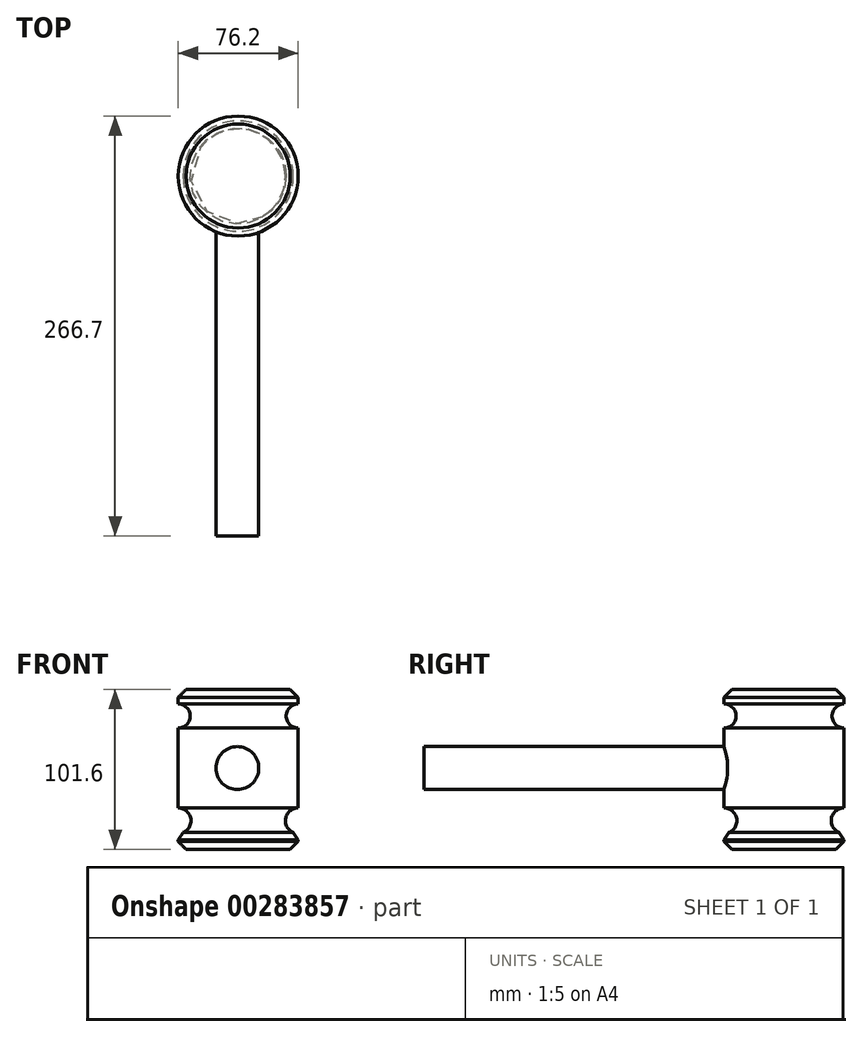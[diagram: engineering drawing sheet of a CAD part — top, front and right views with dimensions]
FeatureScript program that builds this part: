
annotation { "Feature Type Name" : "Feature", "Feature Type Description" : "" }
export const myFeature = defineFeature(function(context is Context, id is Id, definition is map)
    precondition{}
    {
        {
            var Q0;
            Q0=qCreatedBy(makeId("Front.planeOp"),FACE);
            var sketch = newSketch(context, id + "F0", { "sketchPlane" : qUnion([Q0])});
            skLineSegment(sketch, "E0.bottom", {"start": v(-12.75, 61.83) * mm, "end": v(25.35, 61.83) * mm});
            skLineSegment(sketch, "E0.top", {"start": v(-12.75, -39.77) * mm, "end": v(25.35, -39.77) * mm});
            skLineSegment(sketch, "E0.left", {"start": v(-12.75, 61.83) * mm, "end": v(-12.75, 52.57) * mm});
            skLineSegment(sketch, "E0.right", {"start": v(25.35, 61.83) * mm, "end": v(25.35, -39.77) * mm});
            skArc(sketch, "E1", {"start": v(-12.75, -29.67) * mm, "mid": v(-4.63, -21.55) * mm, "end": v(-12.75, -13.43) * mm});
            skArc(sketch, "E2", {"start": v(-12.75, 37.33) * mm, "mid": v(-5.13, 44.95) * mm, "end": v(-12.75, 52.57) * mm});
            skLineSegment(sketch, "E3.trimOffspring", {"start": v(-12.75, -29.67) * mm, "end": v(-12.75, -39.77) * mm});
            skLineSegment(sketch, "E4.trimOffspring", {"start": v(-12.75, 37.33) * mm, "end": v(-12.75, -13.43) * mm});
            skSolve(sketch);
        }
        {
            var Q0;
            Q0 = qSketchRegion(id + "F0", true);
            var Q1;
            Q1=sQuery(id+"F0.wireOp",EDGE,"E0.right");
            revolve(context, id + "F1", {"entities" : qUnion([Q0]), "axis" : qUnion([Q1]), "revolveType" : RevolveType.FULL});
        }
        {
            var Q0;
            Q0=qCreatedBy(makeId("Front.planeOp"),FACE);
            var sketch = newSketch(context, id + "F2", { "sketchPlane" : qUnion([Q0])});
            skCircle(sketch, "E5", {"center": v(24.83, 11.92) * mm, "radius": 13.6 * mm});
            skSolve(sketch);
        }
        {
            var Q0;
            Q0 = qSketchRegion(id + "F2", true);
            extrude(context, id + "F3", {"entities" : qUnion([Q0]), "operationType" : NewBodyOperationType.ADD, "depth" : 228.6 * mm});
        }
        {
            var Q0;
            Q0=makeQuery(id+"F1.opRevolve","SWEPT_FACE",FACE,{"disambiguationData":[OSD([sQuery(id+"F0.wireOp",EDGE,"E0.bottom")])]});
            var Q1;
            Q1=makeQuery(id+"F1.opRevolve","SWEPT_FACE",FACE,{"disambiguationData":[OSD([sQuery(id+"F0.wireOp",EDGE,"E3.trimOffspring")])]});
            chamfer(context, id + "F4", {"entities" : qUnion([Q0, Q1]), "width" : 5.08 * mm, "tangentPropagation" : true});
        }
    });
